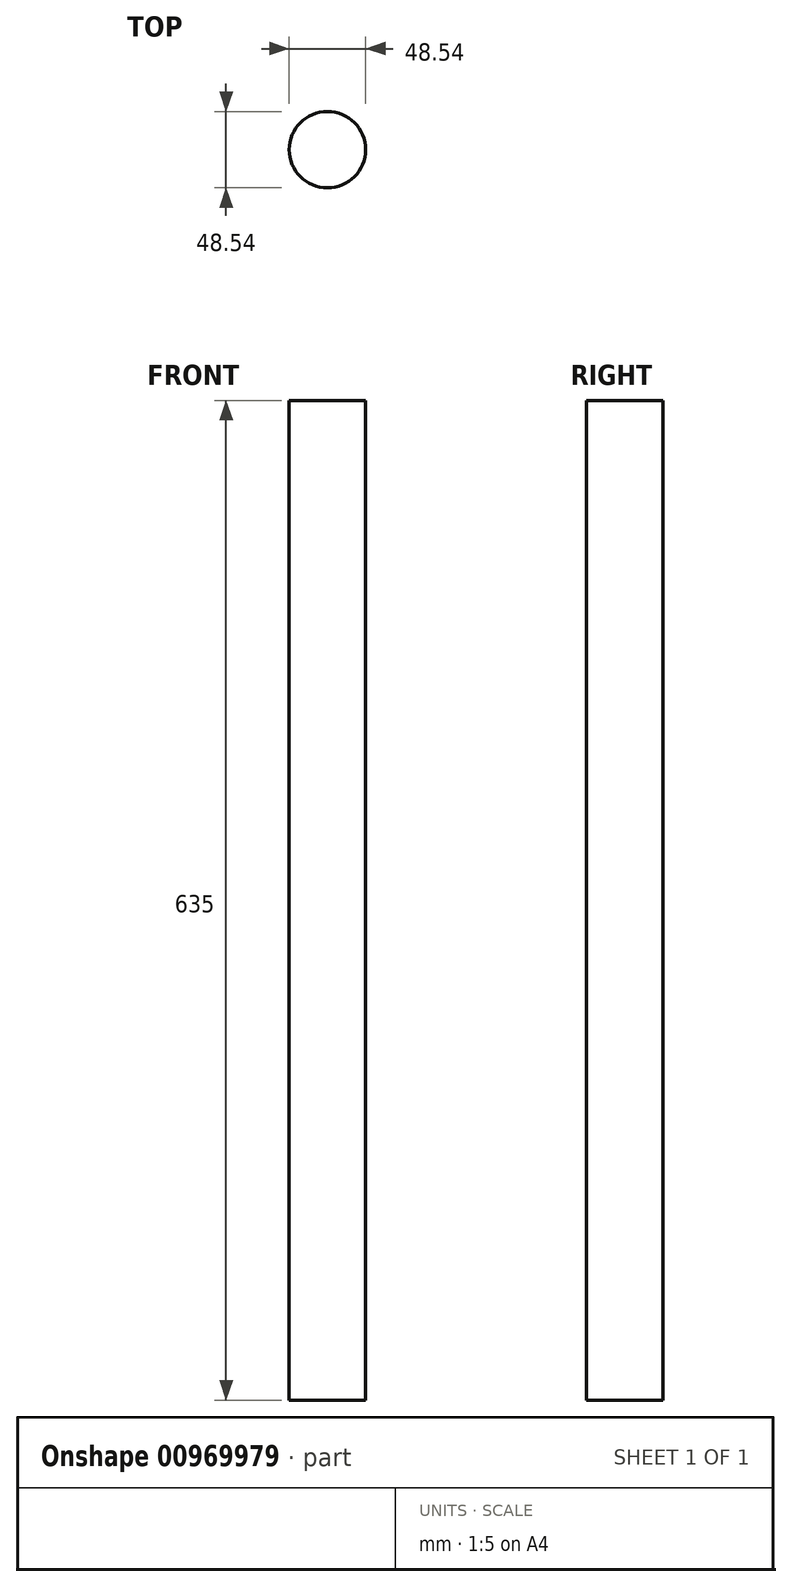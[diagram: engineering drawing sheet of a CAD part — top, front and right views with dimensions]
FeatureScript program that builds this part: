
annotation { "Feature Type Name" : "Feature", "Feature Type Description" : "" }
export const myFeature = defineFeature(function(context is Context, id is Id, definition is map)
    precondition{}
    {
        {
            var Q0;
            Q0=qCreatedBy(makeId("Top.planeOp"),FACE);
            var sketch = newSketch(context, id + "F0", { "sketchPlane" : qUnion([Q0])});
            skCircle(sketch, "E0", {"center": v(0, 0) * mm, "radius": 24.27 * mm});
            skSolve(sketch);
        }
        {
            var Q0;
            Q0 = qSketchRegion(id + "F0", true);
            extrude(context, id + "F1", {"entities" : qUnion([Q0]), "depth" : 635 * mm, "offsetDistance" : 25.4 * mm});
        }
    });
